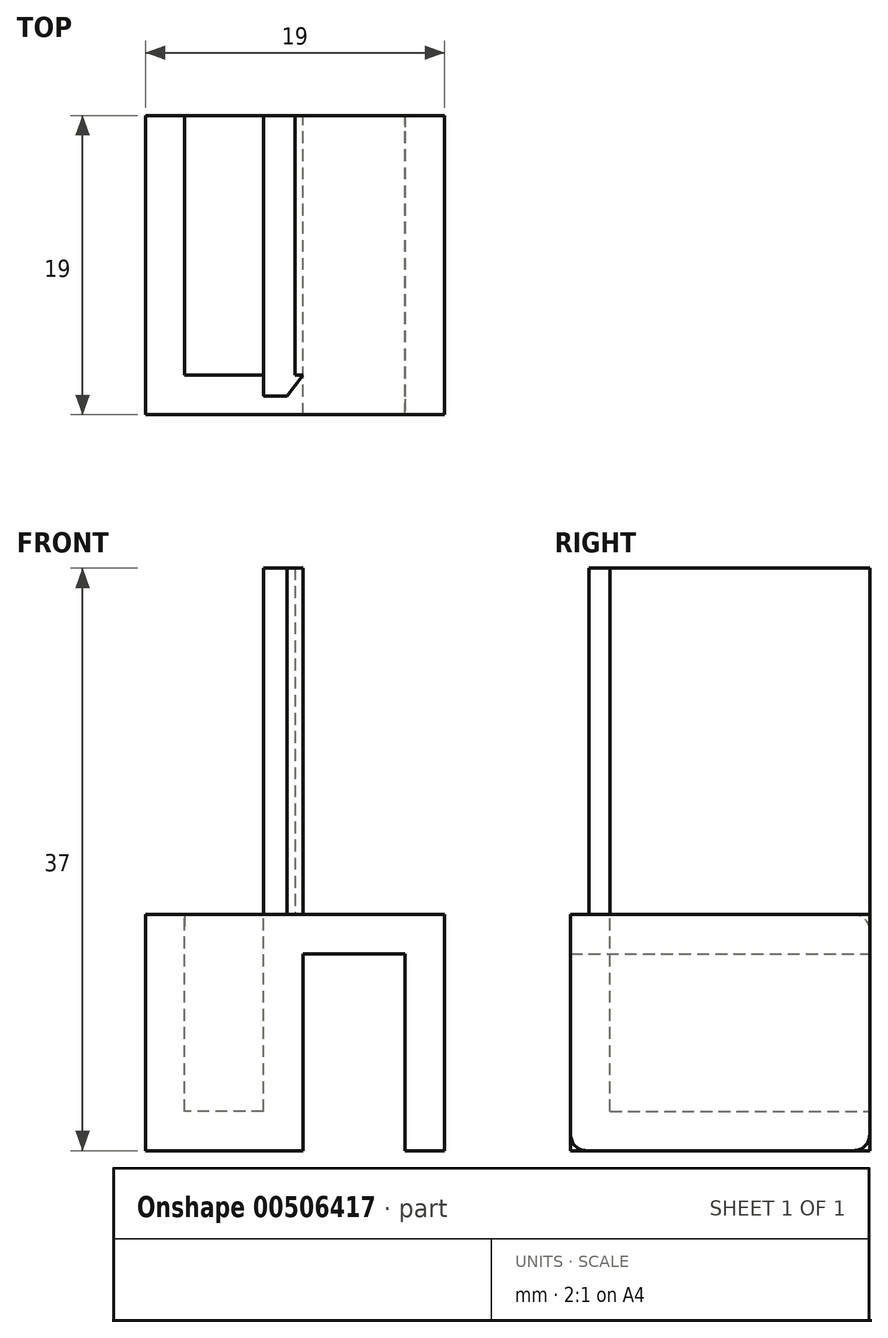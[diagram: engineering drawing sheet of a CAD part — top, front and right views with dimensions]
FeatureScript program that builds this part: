
annotation { "Feature Type Name" : "Feature", "Feature Type Description" : "" }
export const myFeature = defineFeature(function(context is Context, id is Id, definition is map)
    precondition{}
    {
        {
            var Q0;
            Q0=qCreatedBy(makeId("Front.planeOp"),FACE);
            var sketch = newSketch(context, id + "F0", { "sketchPlane" : qUnion([Q0])});
            skLineSegment(sketch, "E0.bottom", {"start": v(-30.43, 15.46) * mm, "end": v(-40.43, 15.46) * mm});
            skLineSegment(sketch, "E0.top", {"start": v(-30.43, 30.46) * mm, "end": v(-40.43, 30.46) * mm});
            skLineSegment(sketch, "E0.left", {"start": v(-30.43, 15.46) * mm, "end": v(-30.43, 30.46) * mm});
            skLineSegment(sketch, "E0.right", {"start": v(-40.43, 15.46) * mm, "end": v(-40.43, 30.46) * mm});
            skPoint(sketch, "E0.middle", {"position": v(-35.43, 22.96) * mm});
            skSolve(sketch);
        }
        {
            var Q0;
            Q0 = qSketchRegion(id + "F0", true);
            extrude(context, id + "F1", {"entities" : qUnion([Q0]), "depth" : 19 * mm});
        }
        {
            var Q0;
            Q0=makeQuery(id+"F1.opExtrude","CAP_FACE",FACE,{"disambiguationData":[OSD([sQuery(id+"F0.wireOp",EDGE,"E0.bottom"),sQuery(id+"F0.wireOp",EDGE,"E0.top"),sQuery(id+"F0.wireOp",EDGE,"E0.left"),sQuery(id+"F0.wireOp",EDGE,"E0.right")])],"isStart":true});
            var Q1;
            Q1=makeQuery(id+"F1.opExtrude","SWEPT_FACE",FACE,{"disambiguationData":[OSD([sQuery(id+"F0.wireOp",EDGE,"E0.top")])]});
            shell(context, id + "F2", {"entities" : qUnion([Q0, Q1]), "thickness" : 2.5 * mm});
        }
        {
            var Q0;
            Q0=makeQuery(id+"F1.opExtrude","SWEPT_FACE",FACE,{"disambiguationData":[OSD([sQuery(id+"F0.wireOp",EDGE,"E0.left")])]});
            extrude(context, id + "F3", {"entities" : qUnion([Q0]), "operationType" : NewBodyOperationType.ADD, "depth" : 9 * mm});
        }
        {
            var Q0;
            {var subQ0=sQuery(id+"F0.wireOp",EDGE,"E0.left");Q0=makeQuery(id+"F3.boolean.opBoolean","MERGE",FACE,{"derivedFrom":[makeQuery(id+"F1.opExtrude","CAP_FACE",FACE,{"disambiguationData":[OSD([sQuery(id+"F0.wireOp",EDGE,"E0.bottom"),sQuery(id+"F0.wireOp",EDGE,"E0.top"),subQ0,sQuery(id+"F0.wireOp",EDGE,"E0.right")])],"isStart":true}),makeQuery(id+"F3.opExtrude","SWEPT_FACE",FACE,{"disambiguationData":[OSD([subQ0]),TDD([makeQuery(id+"F1.opExtrude","CAP_EDGE",EDGE,{"disambiguationData":[OSD([subQ0])],"isStart":true})])]})]});}
            shell(context, id + "F4", {"entities" : qUnion([Q0]), "thickness" : 2.5 * mm});
        }
        {
            var Q0;
            Q0=makeQuery(id+"F4.opShell","OFFSET_FACE",FACE,{"disambiguationData":[OSD([sQuery(id+"F0.wireOp",EDGE,"E0.bottom"),sQuery(id+"F0.wireOp",EDGE,"E0.top"),sQuery(id+"F0.wireOp",EDGE,"E0.left"),sQuery(id+"F0.wireOp",EDGE,"E0.right")])]});
            extrude(context, id + "F5", {"entities" : qUnion([Q0]), "operationType" : NewBodyOperationType.REMOVE, "oppositeDirection" : true, "depth" : 25 * mm});
        }
        {
            var Q0;
            {var subQ0=sQuery(id+"F0.wireOp",EDGE,"E0.left");var subQ1=sQuery(id+"F0.wireOp",EDGE,"E0.bottom");Q0=makeQuery(id+"F5.boolean.opBoolean","MERGE",FACE,{"derivedFrom":[makeQuery(id+"F4.opShell","OFFSET_FACE",FACE,{"disambiguationData":[OSD([subQ1,subQ0])]}),makeQuery(id+"F5.opExtrude","SWEPT_FACE",FACE,{"disambiguationData":[OSD([subQ1,subQ0])]})]});}
            extrude(context, id + "F6", {"entities" : qUnion([Q0]), "operationType" : NewBodyOperationType.REMOVE, "oppositeDirection" : true, "depth" : 25 * mm});
        }
        {
            var Q0;
            {var subQ0=sQuery(id+"F0.wireOp",EDGE,"E0.top");Q0=makeQuery(id+"F3.boolean.opBoolean","MERGE",FACE,{"derivedFrom":[makeQuery(id+"F1.opExtrude","SWEPT_FACE",FACE,{"disambiguationData":[OSD([subQ0])]}),makeQuery(id+"F3.opExtrude","SWEPT_FACE",FACE,{"disambiguationData":[OSD([subQ0,sQuery(id+"F0.wireOp",EDGE,"E0.left")])]})]});}
            var sketch = newSketch(context, id + "F7", { "sketchPlane" : qUnion([Q0])});
            skLineSegment(sketch, "E1", {"start": v(-32.93, 0) * mm, "end": v(-30.93, 0) * mm});
            skLineSegment(sketch, "E2", {"start": v(-32.93, 0) * mm, "end": v(-32.93, -17.82) * mm});
            skLineSegment(sketch, "E3", {"start": v(-30.93, -16.5) * mm, "end": v(-30.43, -16.5) * mm});
            skLineSegment(sketch, "E4", {"start": v(-32.93, -17.82) * mm, "end": v(-31.93, -17.82) * mm});
            skLineSegment(sketch, "E5", {"start": v(-30.93, -16.5) * mm, "end": v(-30.93, 0) * mm});
            skLineSegment(sketch, "E6", {"start": v(-31.93, -17.82) * mm, "end": v(-31.43, -17.82) * mm});
            skLineSegment(sketch, "E7", {"start": v(-31.43, -17.82) * mm, "end": v(-30.43, -16.5) * mm});
            skSolve(sketch);
        }
        {
            var Q0;
            Q0 = qSketchRegion(id + "F7", true);
            extrude(context, id + "F8", {"entities" : qUnion([Q0]), "operationType" : NewBodyOperationType.ADD, "depth" : 22 * mm});
        }
        {
            var Q0;
            {var subQ0=sQuery(id+"F0.wireOp",EDGE,"E0.left");var subQ1=sQuery(id+"F0.wireOp",EDGE,"E0.bottom");var subQ2=makeQuery(id+"F3.opExtrude","CAP_FACE",FACE,{"disambiguationData":[OSD([subQ0])],"isStart":false});Q0=makeQuery(id+"F6.boolean.opBoolean","SPLIT",EDGE,{"disambiguationData":[TD([subQ2])],"derivedFrom":makeQuery(id+"F3.boolean.opBoolean","MERGE",EDGE,{"derivedFrom":[makeQuery(id+"F1.opExtrude","CAP_EDGE",EDGE,{"disambiguationData":[OSD([subQ1])],"isStart":true}),makeQuery(id+"F3.opExtrude","SWEPT_EDGE",EDGE,{"disambiguationData":[OSD([subQ1,subQ0]),TDD([makeQuery(id+"F1.opExtrude","CAP_VERTEX",VERTEX,{"disambiguationData":[OSD([subQ1,subQ0])],"isStart":true})])]})]})});}
            var Q1;
            {var subQ0=sQuery(id+"F0.wireOp",EDGE,"E0.top");Q1=makeQuery(id+"F2.opShell","OFFSET_EDGE",EDGE,{"disambiguationData":[OSD([subQ0]),TDD([makeQuery(id+"F1.opExtrude","CAP_EDGE",EDGE,{"disambiguationData":[OSD([subQ0])],"isStart":true})])]});}
            fillet(context, id + "F9", {"entities" : qUnion([Q0, Q1]), "radius" : 1 * mm, "tangentPropagation" : true, "allowEdgeOverflow" : false});
        }
        {
            var Q0;
            {var subQ0=sQuery(id+"F0.wireOp",EDGE,"E0.left");var subQ1=sQuery(id+"F0.wireOp",EDGE,"E0.bottom");var subQ2=makeQuery(id+"F3.opExtrude","CAP_FACE",FACE,{"disambiguationData":[OSD([subQ0])],"isStart":false});Q0=makeQuery(id+"F6.boolean.opBoolean","SPLIT",EDGE,{"disambiguationData":[TD([subQ2])],"derivedFrom":makeQuery(id+"F3.boolean.opBoolean","MERGE",EDGE,{"derivedFrom":[makeQuery(id+"F1.opExtrude","CAP_EDGE",EDGE,{"disambiguationData":[OSD([subQ1])],"isStart":false}),makeQuery(id+"F3.opExtrude","SWEPT_EDGE",EDGE,{"disambiguationData":[OSD([subQ1,subQ0]),TDD([makeQuery(id+"F1.opExtrude","CAP_VERTEX",VERTEX,{"disambiguationData":[OSD([subQ1,subQ0])],"isStart":false})])]})]})});}
            fillet(context, id + "F10", {"entities" : qUnion([Q0]), "radius" : 1 * mm, "tangentPropagation" : true, "allowEdgeOverflow" : false});
        }
    });
